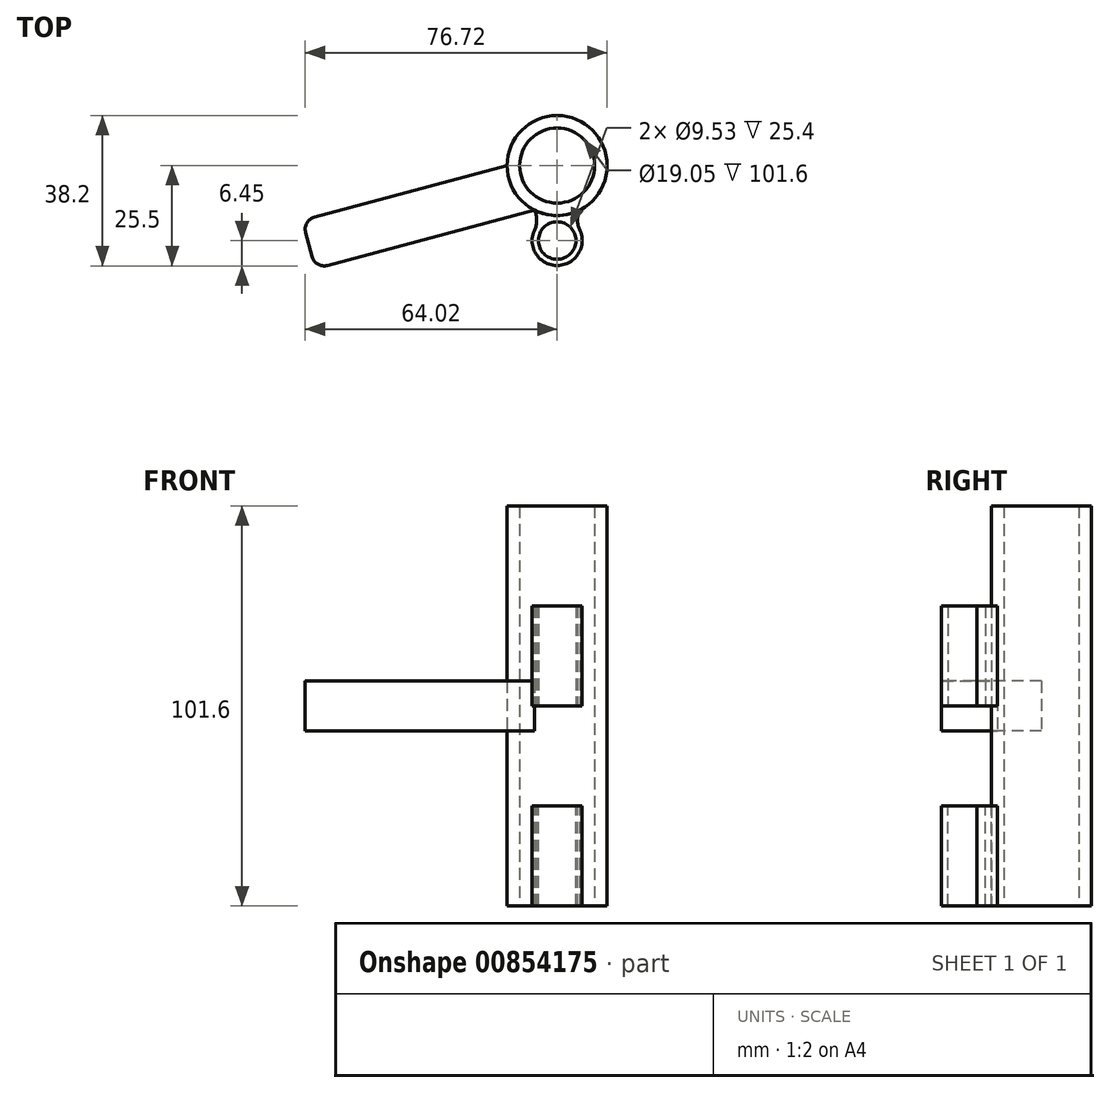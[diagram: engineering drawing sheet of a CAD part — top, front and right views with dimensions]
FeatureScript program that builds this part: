
annotation { "Feature Type Name" : "Feature", "Feature Type Description" : "" }
export const myFeature = defineFeature(function(context is Context, id is Id, definition is map)
    precondition{}
    {
        {
            var Q0;
            Q0=qCreatedBy(makeId("Top.planeOp"),FACE);
            var sketch = newSketch(context, id + "F0", { "sketchPlane" : qUnion([Q0])});
            skCircle(sketch, "E0", {"center": v(0, 0) * mm, "radius": 12.7 * mm});
            skCircle(sketch, "E1", {"center": v(0, 0) * mm, "radius": 9.53 * mm});
            skLineSegment(sketch, "E2", {"start": v(-12.7, 0) * mm, "end": v(-61.67, -13.12) * mm});
            skLineSegment(sketch, "E3", {"start": v(-63.91, -17) * mm, "end": v(-62.27, -23.14) * mm});
            skLineSegment(sketch, "E4", {"start": v(-58.38, -25.39) * mm, "end": v(-5.8, -11.3) * mm});
            skPoint(sketch, "E5.visualSharp", {"position": v(-61.45, -26.2) * mm});
            skArc(sketch, "E5.filletArc", {"start": v(-62.27, -23.14) * mm, "mid": v(-60.79, -25.07) * mm, "end": v(-58.38, -25.39) * mm});
            skPoint(sketch, "E6.visualSharp", {"position": v(-64.73, -13.94) * mm});
            skArc(sketch, "E6.filletArc", {"start": v(-61.67, -13.12) * mm, "mid": v(-63.6, -14.6) * mm, "end": v(-63.91, -17) * mm});
            skPoint(sketch, "E7.end.orphan", {"position": v(0, -9.53) * mm});
            skCircle(sketch, "E8", {"center": v(0, -19.05) * mm, "radius": 6.35 * mm});
            skCircle(sketch, "E9", {"center": v(0, -19.05) * mm, "radius": 4.76 * mm});
            skArc(sketch, "E10", {"start": v(5.8, -11.3) * mm, "mid": v(5.15, -13.88) * mm, "end": v(5.8, -16.46) * mm});
            skArc(sketch, "E11", {"start": v(-5.8, -16.46) * mm, "mid": v(-5.2, -13.88) * mm, "end": v(-5.8, -11.3) * mm});
            skPoint(sketch, "E12.start.orphan", {"position": v(0, -25.4) * mm});
            skSolve(sketch);
        }
        {
            var Q0;
            {var subQ0=sQuery(id+"F0.wireOp",EDGE,"E1");Q0=makeQuery(id+"F0.imprint","IMPRINT",FACE,{"disambiguationData":[TD([[makeQuery(id+"F0.imprint","IMPRINT",EDGE,{"derivedFrom":subQ0}),-1.0]])]});}
            var Q1;
            {var subQ0=sQuery(id+"F0.wireOp",EDGE,"E7");var subQ1=sQuery(id+"F0.wireOp",EDGE,"E0");var subQ2=makeQuery(id+"F0.imprint","INTERSECT",VERTEX,{"derivedFrom":[subQ1,subQ0]});Q1=makeQuery(id+"F0.imprint","IMPRINT",FACE,{"disambiguationData":[TD([[makeQuery(id+"F0.imprint","IMPRINT",EDGE,{"disambiguationData":[TD([[subQ2,1.0]])],"derivedFrom":subQ1}),1.0]])]});}
            var Q2;
            {var subQ0=sQuery(id+"F0.wireOp",EDGE,"MfBvsHdg-jLrl-huXg-2UYU-LDi24QHTvxyt");var subQ1=sQuery(id+"F0.wireOp",EDGE,"E0");var subQ2=makeQuery(id+"F0.imprint","INTERSECT",VERTEX,{"disambiguationData":[OD(0.0)],"derivedFrom":[subQ1,subQ0]});Q2=makeQuery(id+"F0.imprint","IMPRINT",FACE,{"disambiguationData":[TD([[makeQuery(id+"F0.imprint","IMPRINT",EDGE,{"disambiguationData":[TD([[subQ2,-1.0]])],"derivedFrom":subQ1}),1.0]])]});}
            var Q3;
            {var subQ3=sQuery(id+"F0.wireOp",EDGE,"BqvK1fvn-mdkW-RMAl-mkZE-a1791Va0z3hD");Q3=makeQuery(id+"F0.imprint","IMPRINT",FACE,{"disambiguationData":[TD([[makeQuery(id+"F0.imprint","IMPRINT",EDGE,{"derivedFrom":subQ3}),-1.0]])]});}
            extrude(context, id + "F1", {"entities" : qUnion([Q0, Q1, Q2, Q3]), "endBound" : BoundingType.SYMMETRIC, "depth" : 101.6 * mm, "offsetDistance" : 25.4 * mm});
        }
        {
            var Q0;
            {var subQ1=sQuery(id+"F0.wireOp",EDGE,"E2");Q0=makeQuery(id+"F0.imprint","IMPRINT",FACE,{"disambiguationData":[TD([[makeQuery(id+"F0.imprint","IMPRINT",EDGE,{"derivedFrom":subQ1}),1.0]])]});}
            var Q1;
            Q1=makeQuery(id+"F0.imprint","IMPRINT",FACE,{"disambiguationData":[TD([[makeQuery(id+"F0.imprint","IMPRINT",EDGE,{"derivedFrom":sQuery(id+"F0.wireOp",EDGE,"E3")}),1.0]])]});
            extrude(context, id + "F2", {"entities" : qUnion([Q0, Q1]), "operationType" : NewBodyOperationType.ADD, "endBound" : BoundingType.SYMMETRIC, "depth" : 12.7 * mm, "offsetDistance" : 25.4 * mm});
        }
        {
            var Q0;
            {var subQ0=sQuery(id+"F0.wireOp",EDGE,"9lp8qKE7-gRRo-Ce84-AcRP-1Jh8QzfbiSwo");Q0=makeQuery(id+"F0.imprint","IMPRINT",FACE,{"disambiguationData":[TD([[makeQuery(id+"F0.imprint","IMPRINT",EDGE,{"derivedFrom":subQ0}),-1.0]])]});}
            var Q1;
            Q1=makeQuery(id+"F0.imprint","IMPRINT",FACE,{"disambiguationData":[TD([[makeQuery(id+"F0.imprint","IMPRINT",EDGE,{"derivedFrom":sQuery(id+"F0.wireOp",EDGE,"E9")}),-1.0]])]});
            var Q2;
            {var subQ0=sQuery(id+"F0.wireOp",EDGE,"wpij5r65-yGt9-kfeI-sAbr-WvtZKwSm8ecW");var subQ1=sQuery(id+"F0.wireOp",EDGE,"E0");var subQ2=makeQuery(id+"F0.imprint","INTERSECT",VERTEX,{"derivedFrom":[subQ1,subQ0]});Q2=makeQuery(id+"F0.imprint","IMPRINT",FACE,{"disambiguationData":[TD([[makeQuery(id+"F0.imprint","IMPRINT",EDGE,{"disambiguationData":[TD([[subQ2,1.0]])],"derivedFrom":subQ1}),-1.0]])]});}
            var Q3;
            {var subQ0=sQuery(id+"F0.wireOp",EDGE,"E10");var subQ1=sQuery(id+"F0.wireOp",EDGE,"E0");var subQ2=makeQuery(id+"F0.imprint","INTERSECT",VERTEX,{"derivedFrom":[subQ1,subQ0]});Q3=makeQuery(id+"F0.imprint","IMPRINT",FACE,{"disambiguationData":[TD([[makeQuery(id+"F0.imprint","IMPRINT",EDGE,{"disambiguationData":[TD([[subQ2,1.0]])],"derivedFrom":subQ1}),-1.0]])]});}
            var Q4;
            {var subQ0=sQuery(id+"F0.wireOp",EDGE,"E11");var subQ1=sQuery(id+"F0.wireOp",EDGE,"E0");var subQ2=makeQuery(id+"F0.imprint","INTERSECT",VERTEX,{"derivedFrom":[subQ1,subQ0]});Q4=makeQuery(id+"F0.imprint","IMPRINT",FACE,{"disambiguationData":[TD([[makeQuery(id+"F0.imprint","IMPRINT",EDGE,{"disambiguationData":[TD([[subQ2,-1.0]])],"derivedFrom":subQ1}),-1.0]])]});}
            extrude(context, id + "F3", {"entities" : qUnion([Q0, Q1, Q2, Q3, Q4]), "operationType" : NewBodyOperationType.ADD, "oppositeDirection" : true, "depth" : 50.8 * mm, "offsetDistance" : 25.4 * mm});
        }
        {
            var Q0;
            Q0=makeQuery(id+"F0.imprint","IMPRINT",FACE,{"disambiguationData":[TD([[makeQuery(id+"F0.imprint","IMPRINT",EDGE,{"derivedFrom":sQuery(id+"F0.wireOp",EDGE,"E9")}),-1.0]])]});
            var Q1;
            {var subQ0=sQuery(id+"F0.wireOp",EDGE,"E11");var subQ1=sQuery(id+"F0.wireOp",EDGE,"E0");var subQ2=makeQuery(id+"F0.imprint","INTERSECT",VERTEX,{"derivedFrom":[subQ1,subQ0]});Q1=makeQuery(id+"F0.imprint","IMPRINT",FACE,{"disambiguationData":[TD([[makeQuery(id+"F0.imprint","IMPRINT",EDGE,{"disambiguationData":[TD([[subQ2,-1.0]])],"derivedFrom":subQ1}),-1.0]])]});}
            var Q2;
            {var subQ0=sQuery(id+"F0.wireOp",EDGE,"E10");var subQ1=sQuery(id+"F0.wireOp",EDGE,"E0");var subQ2=makeQuery(id+"F0.imprint","INTERSECT",VERTEX,{"derivedFrom":[subQ1,subQ0]});Q2=makeQuery(id+"F0.imprint","IMPRINT",FACE,{"disambiguationData":[TD([[makeQuery(id+"F0.imprint","IMPRINT",EDGE,{"disambiguationData":[TD([[subQ2,1.0]])],"derivedFrom":subQ1}),-1.0]])]});}
            var Q3;
            {var subQ0=sQuery(id+"F0.wireOp",EDGE,"wpij5r65-yGt9-kfeI-sAbr-WvtZKwSm8ecW");var subQ1=sQuery(id+"F0.wireOp",EDGE,"E0");var subQ2=makeQuery(id+"F0.imprint","INTERSECT",VERTEX,{"derivedFrom":[subQ1,subQ0]});Q3=makeQuery(id+"F0.imprint","IMPRINT",FACE,{"disambiguationData":[TD([[makeQuery(id+"F0.imprint","IMPRINT",EDGE,{"disambiguationData":[TD([[subQ2,1.0]])],"derivedFrom":subQ1}),-1.0]])]});}
            extrude(context, id + "F4", {"entities" : qUnion([Q0, Q1, Q2, Q3]), "operationType" : NewBodyOperationType.REMOVE, "oppositeDirection" : true, "depth" : 25.4 * mm, "offsetDistance" : 25.4 * mm});
        }
        {
            var Q0;
            Q0=makeQuery(id+"F0.imprint","IMPRINT",FACE,{"disambiguationData":[TD([[makeQuery(id+"F0.imprint","IMPRINT",EDGE,{"derivedFrom":sQuery(id+"F0.wireOp",EDGE,"E9")}),-1.0]])]});
            var Q1;
            {var subQ0=sQuery(id+"F0.wireOp",EDGE,"E11");var subQ1=sQuery(id+"F0.wireOp",EDGE,"E0");var subQ2=makeQuery(id+"F0.imprint","INTERSECT",VERTEX,{"derivedFrom":[subQ1,subQ0]});Q1=makeQuery(id+"F0.imprint","IMPRINT",FACE,{"disambiguationData":[TD([[makeQuery(id+"F0.imprint","IMPRINT",EDGE,{"disambiguationData":[TD([[subQ2,-1.0]])],"derivedFrom":subQ1}),-1.0]])]});}
            var Q2;
            {var subQ0=sQuery(id+"F0.wireOp",EDGE,"E10");var subQ1=sQuery(id+"F0.wireOp",EDGE,"E0");var subQ2=makeQuery(id+"F0.imprint","INTERSECT",VERTEX,{"derivedFrom":[subQ1,subQ0]});Q2=makeQuery(id+"F0.imprint","IMPRINT",FACE,{"disambiguationData":[TD([[makeQuery(id+"F0.imprint","IMPRINT",EDGE,{"disambiguationData":[TD([[subQ2,1.0]])],"derivedFrom":subQ1}),-1.0]])]});}
            var Q3;
            {var subQ0=sQuery(id+"F0.wireOp",EDGE,"wpij5r65-yGt9-kfeI-sAbr-WvtZKwSm8ecW");var subQ1=sQuery(id+"F0.wireOp",EDGE,"E0");var subQ2=makeQuery(id+"F0.imprint","INTERSECT",VERTEX,{"derivedFrom":[subQ1,subQ0]});Q3=makeQuery(id+"F0.imprint","IMPRINT",FACE,{"disambiguationData":[TD([[makeQuery(id+"F0.imprint","IMPRINT",EDGE,{"disambiguationData":[TD([[subQ2,1.0]])],"derivedFrom":subQ1}),-1.0]])]});}
            extrude(context, id + "F5", {"entities" : qUnion([Q0, Q1, Q2, Q3]), "operationType" : NewBodyOperationType.ADD, "depth" : 25.4 * mm, "offsetDistance" : 25.4 * mm});
        }
    });
